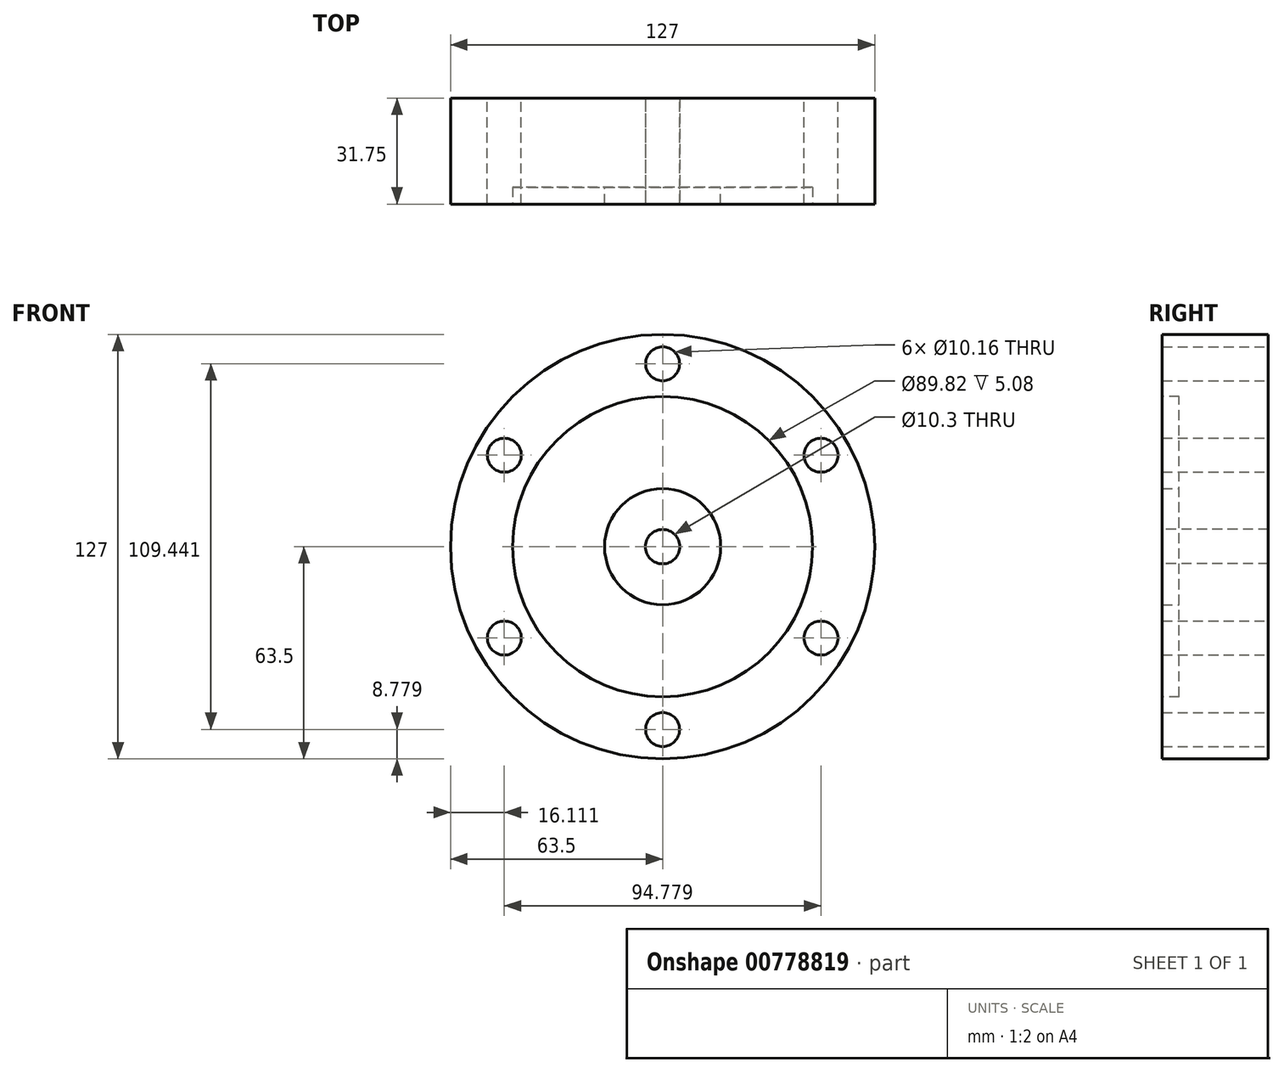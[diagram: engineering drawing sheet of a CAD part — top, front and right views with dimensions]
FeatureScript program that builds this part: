
annotation { "Feature Type Name" : "Feature", "Feature Type Description" : "" }
export const myFeature = defineFeature(function(context is Context, id is Id, definition is map)
    precondition{}
    {
        {
            var Q0;
            Q0=qCreatedBy(makeId("Front.planeOp"),FACE);
            var sketch = newSketch(context, id + "F0", { "sketchPlane" : qUnion([Q0])});
            skCircle(sketch, "E0", {"center": v(0, 0) * mm, "radius": 63.5 * mm});
            skCircle(sketch, "E1", {"center": v(0, 54.72) * mm, "radius": 5.08 * mm});
            skCircle(sketch, "E2.1.0", {"center": v(-47.39, 27.36) * mm, "radius": 5.08 * mm});
            skCircle(sketch, "E2.2.0", {"center": v(-47.39, -27.36) * mm, "radius": 5.08 * mm});
            skCircle(sketch, "E2.3.0", {"center": v(0, -54.72) * mm, "radius": 5.08 * mm});
            skCircle(sketch, "E2.4.0", {"center": v(47.39, -27.36) * mm, "radius": 5.08 * mm});
            skCircle(sketch, "E2.5.0", {"center": v(47.39, 27.36) * mm, "radius": 5.08 * mm});
            skSolve(sketch);
        }
        {
            var Q0;
            Q0 = qSketchRegion(id + "F0", true);
            extrude(context, id + "F1", {"entities" : qUnion([Q0]), "depth" : 31.75 * mm, "offsetDistance" : 25.4 * mm});
        }
        {
            var Q0;
            Q0=makeQuery(id+"F1.opExtrude","CAP_FACE",FACE,{"disambiguationData":[OSD([sQuery(id+"F0.wireOp",EDGE,"E0"),sQuery(id+"F0.wireOp",EDGE,"E1"),sQuery(id+"F0.wireOp",EDGE,"E2.1.0"),sQuery(id+"F0.wireOp",EDGE,"E2.2.0"),sQuery(id+"F0.wireOp",EDGE,"E2.3.0"),sQuery(id+"F0.wireOp",EDGE,"E2.4.0"),sQuery(id+"F0.wireOp",EDGE,"E2.5.0")])],"isStart":false});
            var sketch = newSketch(context, id + "F2", { "sketchPlane" : qUnion([Q0])});
            skCircle(sketch, "E3", {"center": v(0, 0) * mm, "radius": 44.9 * mm});
            skSolve(sketch);
        }
        {
            var Q0;
            Q0 = qSketchRegion(id + "F2", true);
            extrude(context, id + "F3", {"entities" : qUnion([Q0]), "operationType" : NewBodyOperationType.REMOVE, "oppositeDirection" : true, "depth" : 5.08 * mm, "offsetDistance" : 25.4 * mm});
        }
        {
            var Q0;
            Q0=makeQuery(id+"F3.boolean.opBoolean","COPY",FACE,{"derivedFrom":makeQuery(id+"F3.opExtrude","CAP_FACE",FACE,{"disambiguationData":[OSD([sQuery(id+"F2.wireOp",EDGE,"E3")])],"isStart":false})});
            var sketch = newSketch(context, id + "F4", { "sketchPlane" : qUnion([Q0])});
            skCircle(sketch, "E4", {"center": v(0, 0) * mm, "radius": 17.39 * mm});
            skSolve(sketch);
        }
        {
            var Q0;
            Q0 = qSketchRegion(id + "F4", true);
            extrude(context, id + "F5", {"entities" : qUnion([Q0]), "operationType" : NewBodyOperationType.ADD, "depth" : 5.08 * mm, "offsetDistance" : 25.4 * mm});
        }
        {
            var Q0;
            Q0=makeQuery(id+"F5.opExtrude","CAP_FACE",FACE,{"disambiguationData":[OSD([sQuery(id+"F4.wireOp",EDGE,"E4")])],"isStart":false});
            var sketch = newSketch(context, id + "F6", { "sketchPlane" : qUnion([Q0])});
            skPoint(sketch, "E5", {"position": v(0, 0) * mm});
            skSolve(sketch);
        }
        {
            var Q0;
            Q0=sQuery(id+"F6.wireOp",VERTEX,"E5");
            var Q1;
            Q1=makeQuery(id+"F1.opExtrude","SWEPT_BODY",BODY,{"disambiguationData":[OSD([sQuery(id+"F0.wireOp",EDGE,"E0"),sQuery(id+"F0.wireOp",EDGE,"E1"),sQuery(id+"F0.wireOp",EDGE,"E2.1.0"),sQuery(id+"F0.wireOp",EDGE,"E2.2.0"),sQuery(id+"F0.wireOp",EDGE,"E2.3.0"),sQuery(id+"F0.wireOp",EDGE,"E2.4.0"),sQuery(id+"F0.wireOp",EDGE,"E2.5.0")])]});
            hole(context, id + "F7", {"style" : HoleStyle.SIMPLE, "endStyle" : HoleEndStyle.BLIND, "standardTappedOrClearance" : lookupTablePath({ "standard" : "ISO", "engagement" : "75%", "pitch" : "1.75 mm", "size" : "M12", "type" : "Tapped" }), "standardBlindInLast" : lookupTablePath({ "standard" : "ISO", "engagement" : "75%", "pitch" : "1.75 mm", "size" : "M12", "type" : "Tapped" }), "holeDiameter" : 10.3 * mm, "majorDiameter" : 12 * mm, "showTappedDepth" : true, "holeDepth" : 81.46 * mm, "tappedDepth" : 76.2 * mm, "tapClearance" : 3, "startFromSketch" : true, "locations" : qUnion([Q0]), "scope" : qUnion([Q1])});
        }
    });
